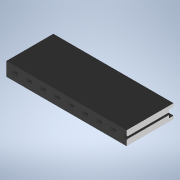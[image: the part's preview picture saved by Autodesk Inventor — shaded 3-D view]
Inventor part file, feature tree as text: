
AUTODESK INVENTOR PART (.ipt)
format: ipt  version: 2021 (Build 250183000, 183)  size: 355,328 bytes
history: native  units: in
note: dims shown in document units (in); Inventor stores cm internally (conversion verified against a paired STEP export)
features: other x1, extrude x1, sketch x1
ambient origin geometry x8: Origin, YZ Plane, XZ Plane, XY Plane, X Axis, Y Axis, Z Axis, Center Point
bodies: Solid1 (feature_tree)
feature tree (3):
  other  "71071773_33.ipt"
  extrude  "Extrusion1"  [1 undecoded]
  sketch  "Sketch1"  dims[d0=2.4in d1=0.0in]
note: 1 required parameter value undecoded (feature->parameter linkage not recoverable at this tier; creation-order binding heuristic only, values carry confidence <= 0.55)
